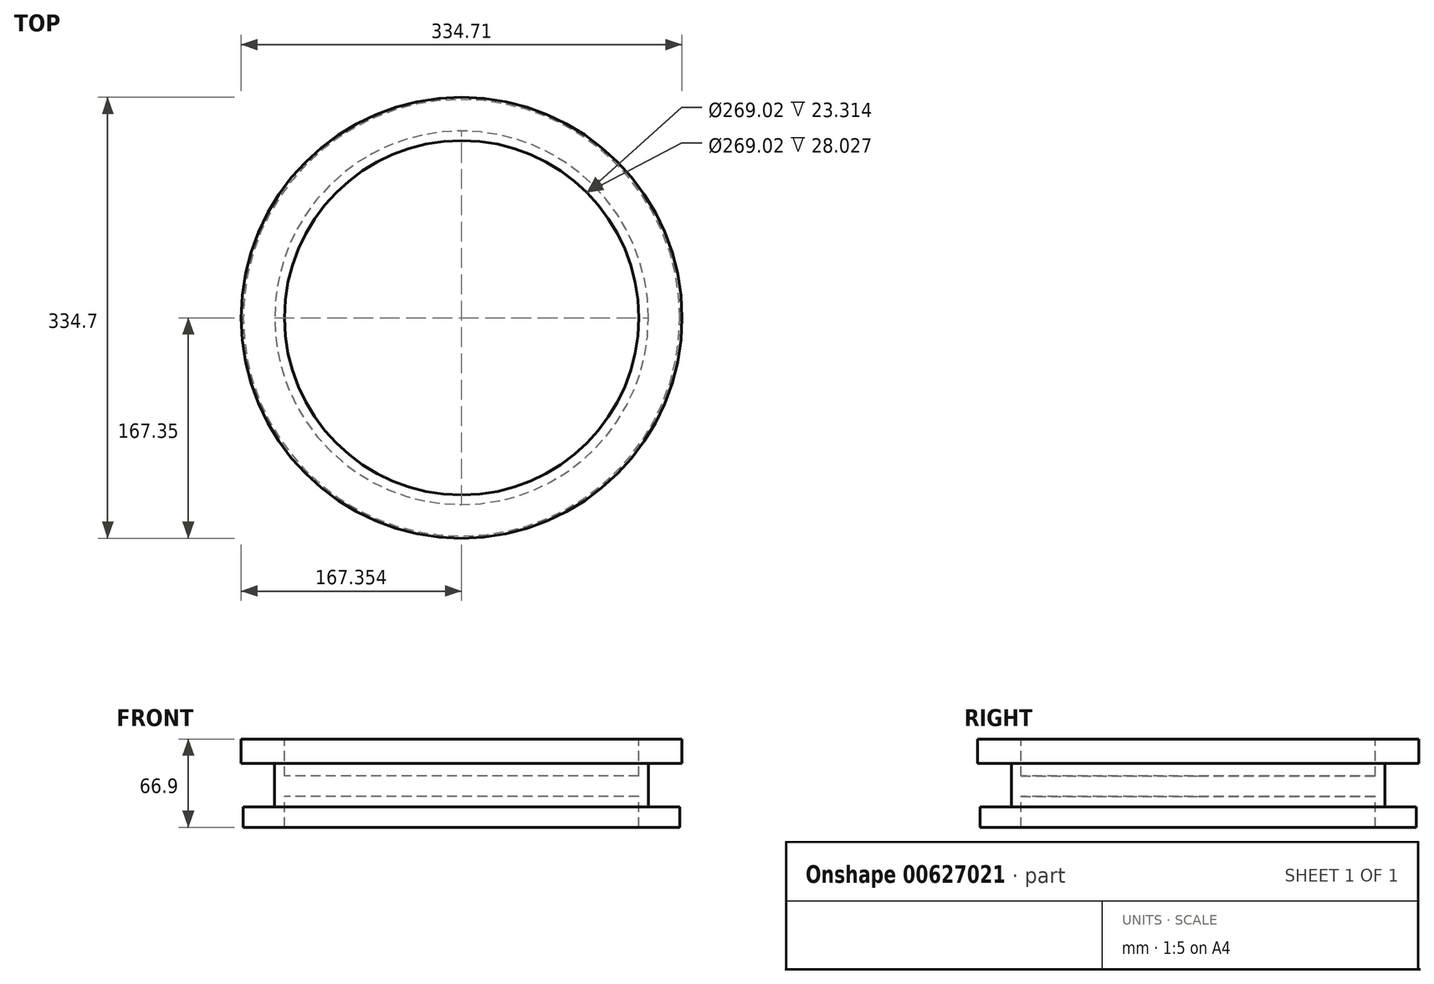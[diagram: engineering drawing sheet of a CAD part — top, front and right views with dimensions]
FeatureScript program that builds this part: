
annotation { "Feature Type Name" : "Feature", "Feature Type Description" : "" }
export const myFeature = defineFeature(function(context is Context, id is Id, definition is map)
    precondition{}
    {
        {
            var Q0;
            Q0=qCreatedBy(makeId("Front.planeOp"),FACE);
            var sketch = newSketch(context, id + "F0", { "sketchPlane" : qUnion([Q0])});
            skLineSegment(sketch, "E0.bottom", {"start": v(69.25, 47.7) * mm, "end": v(61.93, 47.7) * mm});
            skLineSegment(sketch, "E0.top", {"start": v(69.25, -19.2) * mm, "end": v(61.93, -19.2) * mm});
            skLineSegment(sketch, "E0.left", {"start": v(69.25, 47.7) * mm, "end": v(69.25, -19.2) * mm});
            skLineSegment(sketch, "E0.right", {"start": v(61.93, 47.7) * mm, "end": v(61.93, -19.2) * mm});
            skLineSegment(sketch, "E1.bottom", {"start": v(61.93, 19.68) * mm, "end": v(-72.59, 19.68) * mm});
            skLineSegment(sketch, "E1.top", {"start": v(61.93, 4.11) * mm, "end": v(-72.59, 4.11) * mm});
            skLineSegment(sketch, "E1.left", {"start": v(61.93, 19.68) * mm, "end": v(61.93, 4.11) * mm});
            skLineSegment(sketch, "E1.right", {"start": v(-72.59, 19.68) * mm, "end": v(-72.59, 4.11) * mm});
            skLineSegment(sketch, "E2.bottom", {"start": v(69.25, 47.7) * mm, "end": v(94.77, 47.7) * mm});
            skLineSegment(sketch, "E2.top", {"start": v(69.25, 29.17) * mm, "end": v(94.77, 29.17) * mm});
            skLineSegment(sketch, "E2.left", {"start": v(69.25, 47.7) * mm, "end": v(69.25, 29.17) * mm});
            skLineSegment(sketch, "E2.right", {"start": v(94.77, 47.7) * mm, "end": v(94.77, 29.17) * mm});
            skLineSegment(sketch, "E3.bottom", {"start": v(69.25, -19.2) * mm, "end": v(93.08, -19.2) * mm});
            skLineSegment(sketch, "E3.top", {"start": v(69.25, -3.7) * mm, "end": v(93.08, -3.7) * mm});
            skLineSegment(sketch, "E3.left", {"start": v(69.25, -19.2) * mm, "end": v(69.25, -3.7) * mm});
            skLineSegment(sketch, "E3.right", {"start": v(93.08, -19.2) * mm, "end": v(93.08, -3.7) * mm});
            skSolve(sketch);
        }
        {
            var Q0;
            Q0=makeQuery(id+"F0.imprint","IMPRINT",FACE,{"disambiguationData":[TD([[makeQuery(id+"F0.imprint","IMPRINT",EDGE,{"derivedFrom":sQuery(id+"F0.wireOp",EDGE,"E1.bottom")}),1.0]])]});
            var Q1;
            {var subQ1=sQuery(id+"F0.wireOp",EDGE,"E0.bottom");Q1=makeQuery(id+"F0.imprint","IMPRINT",FACE,{"disambiguationData":[TD([[makeQuery(id+"F0.imprint","IMPRINT",EDGE,{"derivedFrom":subQ1}),1.0]])]});}
            var Q2;
            Q2=makeQuery(id+"F0.imprint","IMPRINT",FACE,{"disambiguationData":[TD([[makeQuery(id+"F0.imprint","IMPRINT",EDGE,{"derivedFrom":sQuery(id+"F0.wireOp",EDGE,"E2.bottom")}),-1.0]])]});
            var Q3;
            Q3=makeQuery(id+"F0.imprint","IMPRINT",FACE,{"disambiguationData":[TD([[makeQuery(id+"F0.imprint","IMPRINT",EDGE,{"derivedFrom":sQuery(id+"F0.wireOp",EDGE,"E3.bottom")}),1.0]])]});
            var Q4;
            Q4=sQuery(id+"F0.wireOp",EDGE,"E1.right");
            revolve(context, id + "F1", {"entities" : qUnion([Q0, Q1, Q2, Q3]), "axis" : qUnion([Q4]), "revolveType" : RevolveType.FULL});
        }
    });
